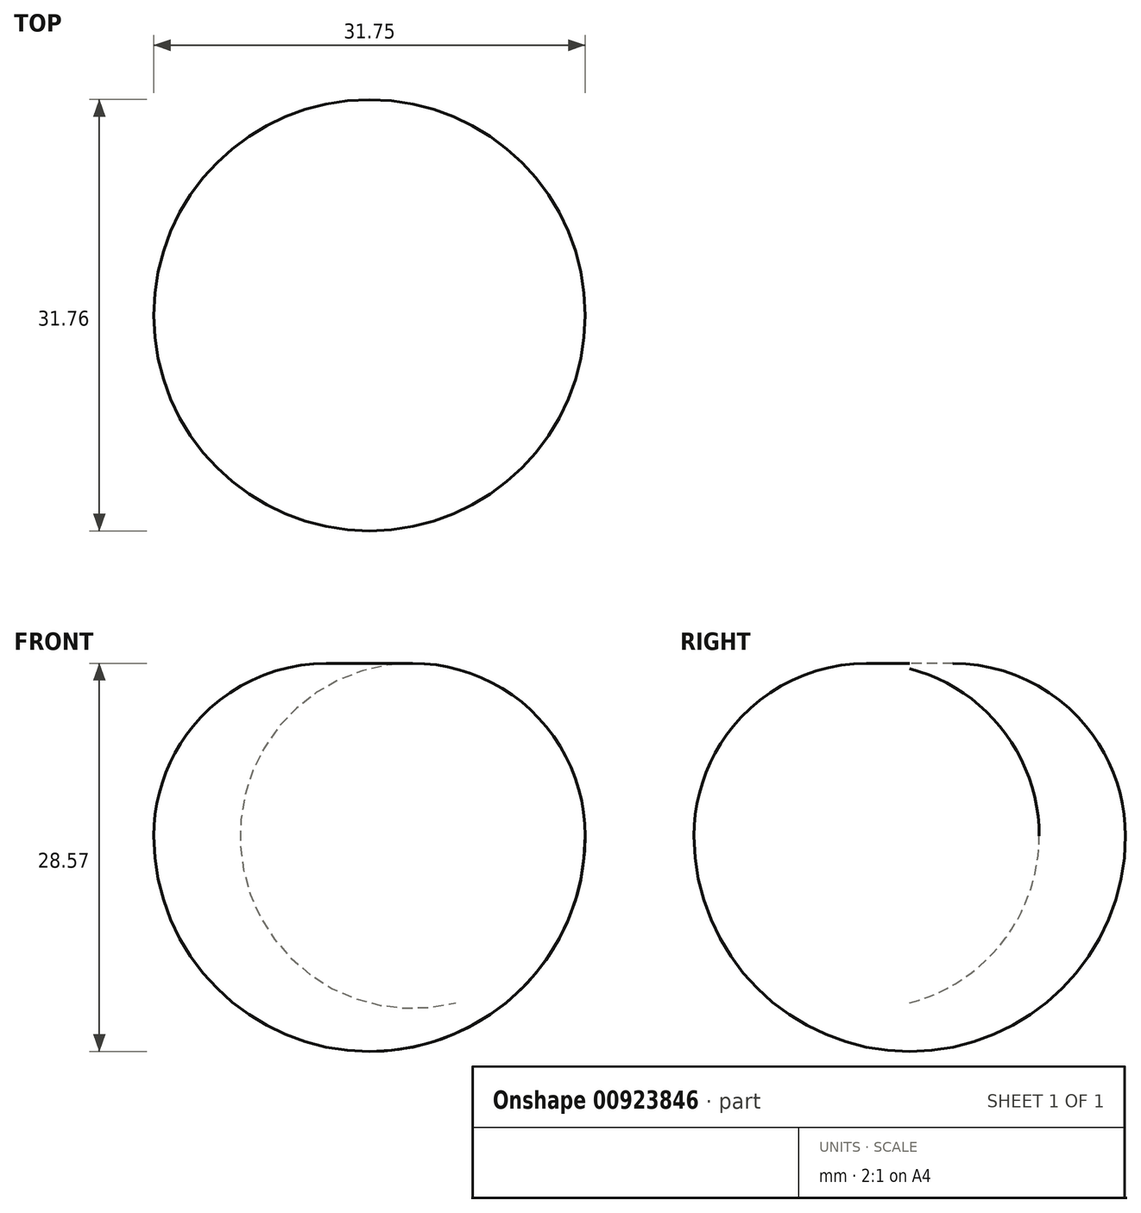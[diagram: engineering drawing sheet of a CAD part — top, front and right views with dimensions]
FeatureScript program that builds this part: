
annotation { "Feature Type Name" : "Feature", "Feature Type Description" : "" }
export const myFeature = defineFeature(function(context is Context, id is Id, definition is map)
    precondition{}
    {
        {
            var Q0;
            Q0=qCreatedBy(makeId("Front.planeOp"),FACE);
            var sketch = newSketch(context, id + "F0", { "sketchPlane" : qUnion([Q0])});
            skLineSegment(sketch, "E0", {"start": v(3.18, 0) * mm, "end": v(6.35, 0) * mm});
            skArc(sketch, "E1", {"start": v(19.05, 0) * mm, "mid": v(14.13, 10.04) * mm, "end": v(3.18, 12.3) * mm});
            skPoint(sketch, "E2.orphan", {"position": v(12.7, 0) * mm});
            skArc(sketch, "E3", {"start": v(3.18, -15.87) * mm, "mid": v(14.4, -11.23) * mm, "end": v(19.05, 0) * mm});
            skLineSegment(sketch, "E4", {"start": v(3.18, 12.3) * mm, "end": v(3.18, -15.87) * mm});
            skPoint(sketch, "E5.orphan", {"position": v(0, 0) * mm});
            skArc(sketch, "E6", {"start": v(28.57, 51.6) * mm, "mid": v(10.08, 35.7) * mm, "end": v(3.18, 12.3) * mm});
            skArc(sketch, "E7", {"start": v(28.57, 50.11) * mm, "mid": v(10.63, 35.15) * mm, "end": v(4.6, 12.58) * mm});
            skLineSegment(sketch, "E8", {"start": v(28.57, 51.6) * mm, "end": v(28.57, 50.11) * mm});
            skSolve(sketch);
        }
        {
            var Q0;
            {var subQ0=sQuery(id+"F0.wireOp",EDGE,"E1");Q0=makeQuery(id+"F0.imprint","IMPRINT",FACE,{"disambiguationData":[TD([[makeQuery(id+"F0.imprint","IMPRINT",EDGE,{"derivedFrom":subQ0}),1.0]])]});}
            var Q1;
            Q1=sQuery(id+"F0.wireOp",EDGE,"E4");
            revolve(context, id + "F1", {"surfaceOperationType" : NewSurfaceOperationType.NEW, "entities" : qUnion([Q0]), "axis" : qUnion([Q1]), "revolveType" : RevolveType.FULL});
        }
    });
